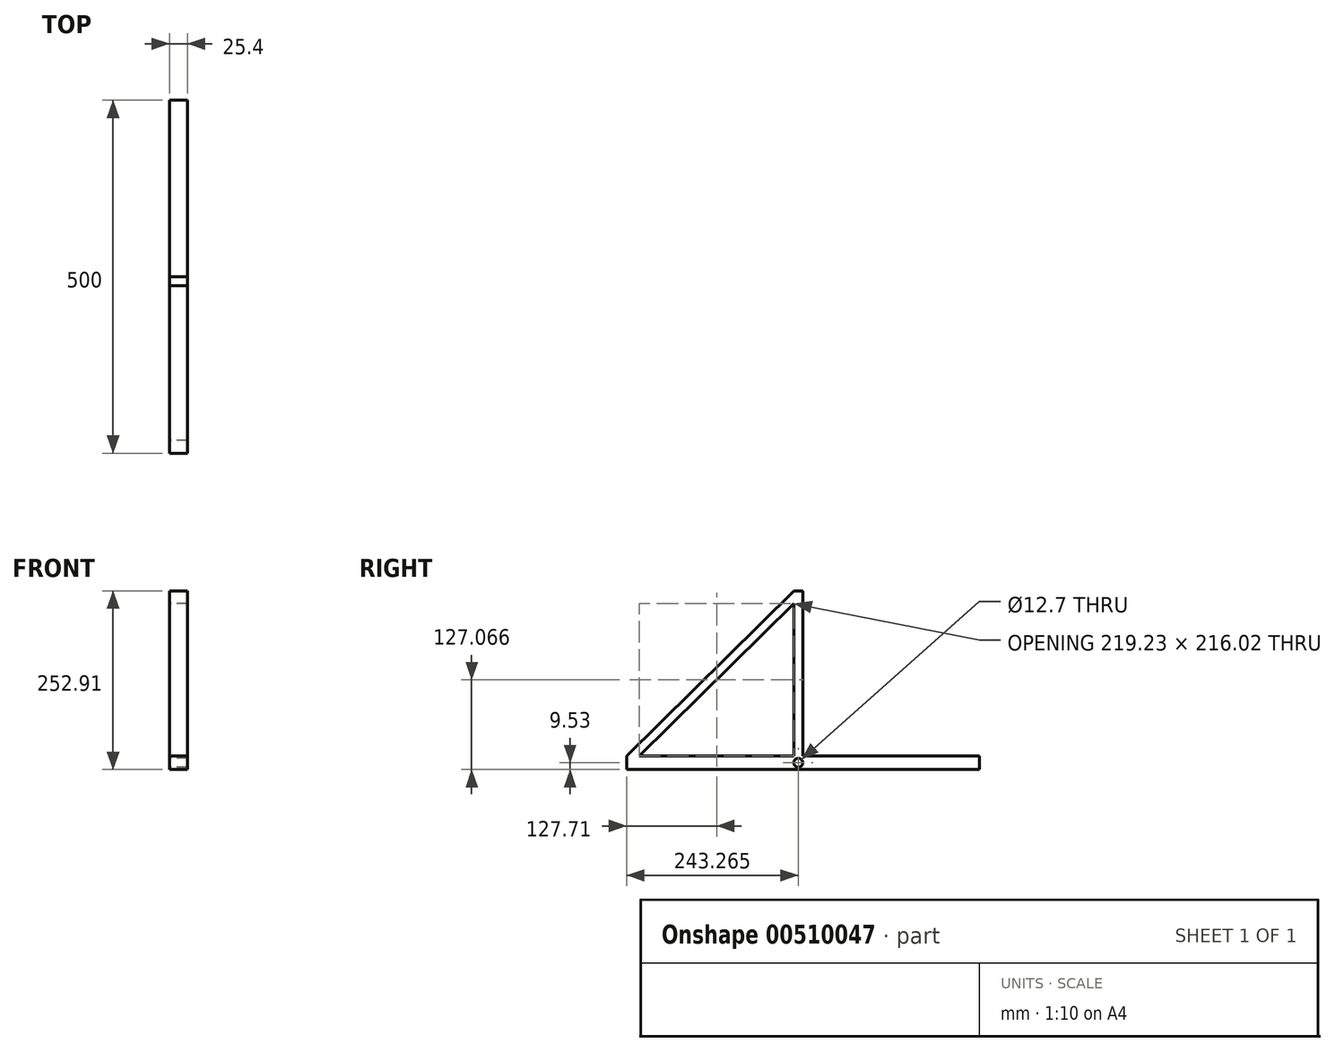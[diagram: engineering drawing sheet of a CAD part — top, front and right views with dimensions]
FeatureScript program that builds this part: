
annotation { "Feature Type Name" : "Feature", "Feature Type Description" : "" }
export const myFeature = defineFeature(function(context is Context, id is Id, definition is map)
    precondition{}
    {
        {
            var Q0;
            Q0=qCreatedBy(makeId("Right.planeOp"),FACE);
            var sketch = newSketch(context, id + "F0", { "sketchPlane" : qUnion([Q0])});
            skLineSegment(sketch, "E0.bottom", {"start": v(-250, 9.52) * mm, "end": v(250, 9.52) * mm});
            skLineSegment(sketch, "E0.top", {"start": v(-250, -9.52) * mm, "end": v(250, -9.52) * mm});
            skLineSegment(sketch, "E0.left", {"start": v(-250, 9.52) * mm, "end": v(-250, -9.52) * mm});
            skLineSegment(sketch, "E0.right", {"start": v(250, 9.52) * mm, "end": v(250, -9.52) * mm});
            skPoint(sketch, "E0.middle", {"position": v(0, 0) * mm});
            skLineSegment(sketch, "E1.0", {"start": v(0.03, 3.56) * mm, "end": v(0.03, -6.66) * mm});
            skLineSegment(sketch, "E2.bottom", {"start": v(0.03, -6.66) * mm, "end": v(-12.67, -6.66) * mm});
            skLineSegment(sketch, "E2.top", {"start": v(0.03, 243.38) * mm, "end": v(-12.67, 243.38) * mm});
            skLineSegment(sketch, "E2.left", {"start": v(0.03, -6.66) * mm, "end": v(0.03, 243.38) * mm});
            skLineSegment(sketch, "E2.right", {"start": v(-12.67, -6.66) * mm, "end": v(-12.67, 243.38) * mm});
            skLineSegment(sketch, "E3", {"start": v(-12.67, 243.38) * mm, "end": v(-250, 9.52) * mm});
            skLineSegment(sketch, "E4.0", {"start": v(-12.67, 225.55) * mm, "end": v(-231.97, 9.47) * mm});
            skLineSegment(sketch, "E5", {"start": v(-231.97, 9.47) * mm, "end": v(-12.67, 225.55) * mm});
            skPoint(sketch, "E6.0.start.orphan", {"position": v(-237.24, 9.47) * mm});
            skCircle(sketch, "E7", {"center": v(-6.74, 0) * mm, "radius": 6.35 * mm});
            skSolve(sketch);
        }
        {
            var Q0;
            Q0=qSketchRegion(id+"F0",true);
            extrude(context, id + "F1", {"entities" : qUnion([Q0]), "depth" : 25.4 * mm});
        }
    });
